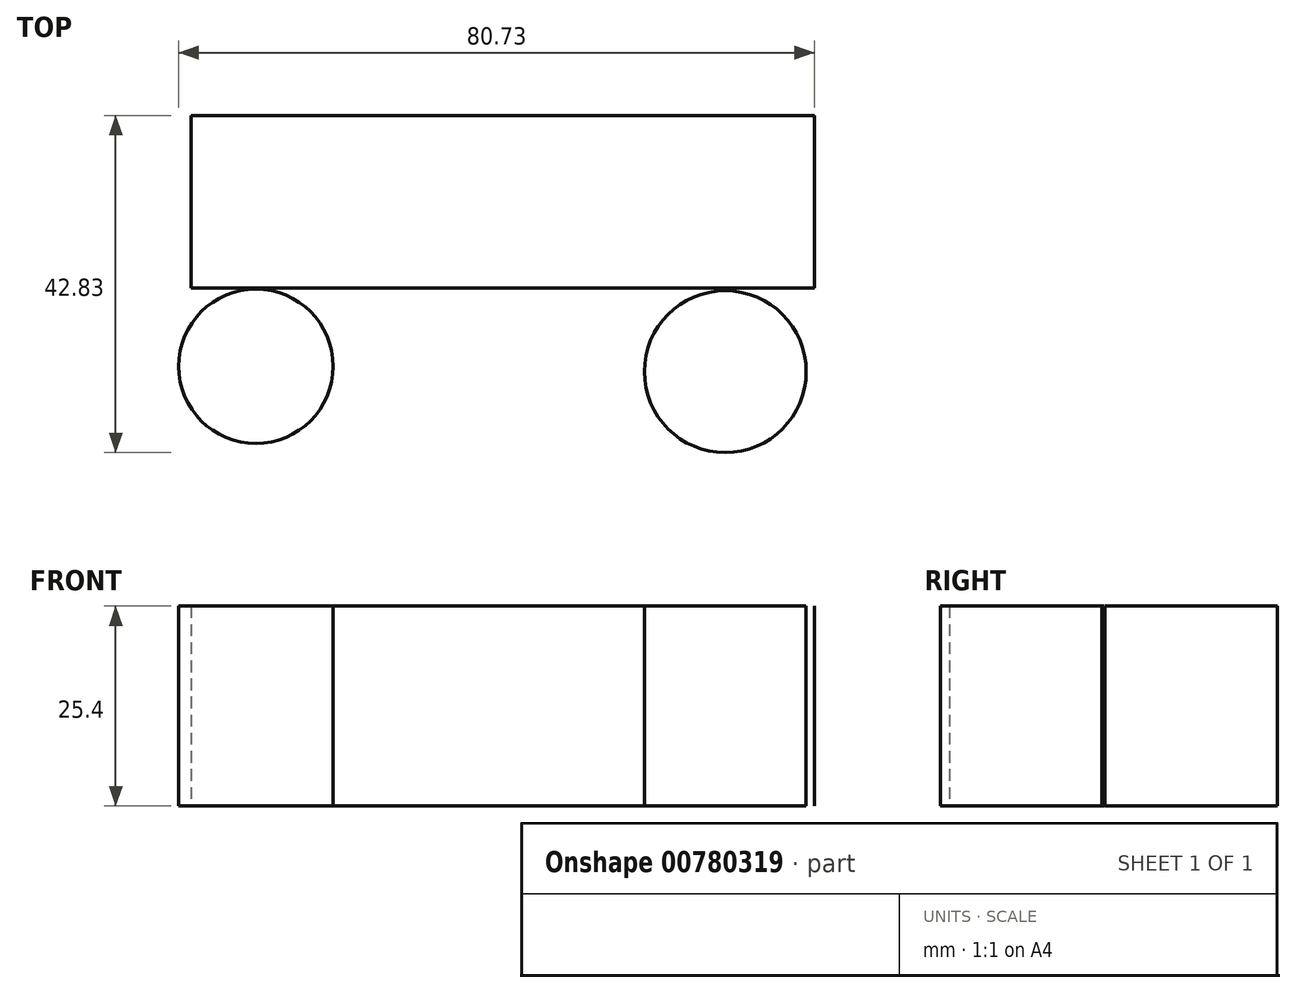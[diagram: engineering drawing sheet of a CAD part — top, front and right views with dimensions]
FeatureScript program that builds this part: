
annotation { "Feature Type Name" : "Feature", "Feature Type Description" : "" }
export const myFeature = defineFeature(function(context is Context, id is Id, definition is map)
    precondition{}
    {
        {
            var Q0;
            Q0=qCreatedBy(makeId("Top.planeOp"),FACE);
            var sketch = newSketch(context, id + "F0", { "sketchPlane" : qUnion([Q0])});
            skLineSegment(sketch, "E0.bottom", {"start": v(-39.58, 10.96) * mm, "end": v(39.58, 10.96) * mm});
            skLineSegment(sketch, "E0.top", {"start": v(-39.58, -10.96) * mm, "end": v(39.58, -10.96) * mm});
            skLineSegment(sketch, "E0.left", {"start": v(-39.58, 10.96) * mm, "end": v(-39.58, -10.96) * mm});
            skLineSegment(sketch, "E0.right", {"start": v(39.58, 10.96) * mm, "end": v(39.58, -10.96) * mm});
            skPoint(sketch, "E0.middle", {"position": v(0, 0) * mm});
            skSolve(sketch);
        }
        {
            var Q0;
            Q0=makeQuery(id+"F0.imprint","IMPRINT",FACE,{"disambiguationData":[TD([[makeQuery(id+"F0.imprint","IMPRINT",EDGE,{"derivedFrom":sQuery(id+"F0.wireOp",EDGE,"E0.bottom")}),-1.0]])]});
            extrude(context, id + "F1", {"entities" : qUnion([Q0]), "depth" : 25.4 * mm, "offsetDistance" : 25.4 * mm});
        }
        {
            var Q0;
            Q0=qCreatedBy(makeId("Top.planeOp"),FACE);
            var sketch = newSketch(context, id + "F2", { "sketchPlane" : qUnion([Q0])});
            skCircle(sketch, "E1", {"center": v(-31.35, -20.9) * mm, "radius": 9.8 * mm});
            skCircle(sketch, "E2", {"center": v(28.27, -21.59) * mm, "radius": 10.28 * mm});
            skSolve(sketch);
        }
        {
            var Q0;
            Q0=makeQuery(id+"F2.imprint","IMPRINT",FACE,{"disambiguationData":[TD([[makeQuery(id+"F2.imprint","IMPRINT",EDGE,{"derivedFrom":sQuery(id+"F2.wireOp",EDGE,"E1")}),1.0]])]});
            var Q1;
            Q1=makeQuery(id+"F2.imprint","IMPRINT",FACE,{"disambiguationData":[TD([[makeQuery(id+"F2.imprint","IMPRINT",EDGE,{"derivedFrom":sQuery(id+"F2.wireOp",EDGE,"E2")}),1.0]])]});
            extrude(context, id + "F3", {"entities" : qUnion([Q0, Q1]), "depth" : 25.4 * mm, "offsetDistance" : 25.4 * mm});
        }
    });
